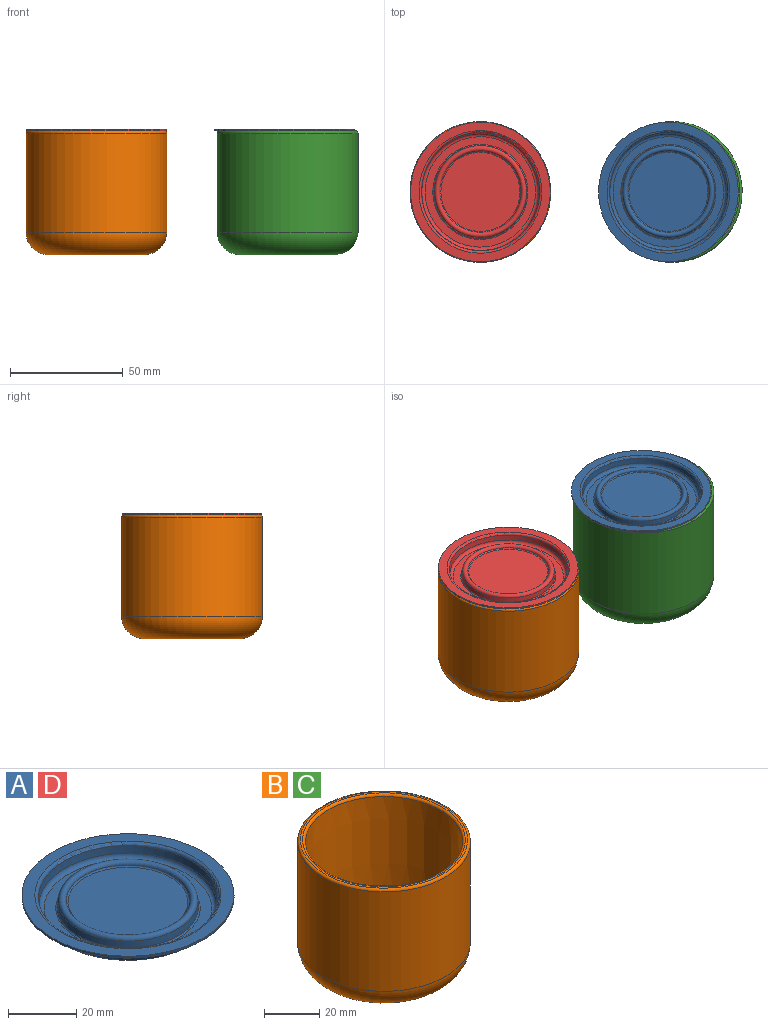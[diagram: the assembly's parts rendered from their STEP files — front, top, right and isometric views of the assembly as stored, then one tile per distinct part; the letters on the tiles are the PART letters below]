
ASSEMBLY  parts=4 mates=4
PART A: 22 faces, bbox 62x62x5.5 mm
  f0: plane 35.45x35.45mm, normal (0,0,-1), area 987mm2, adj f17
  f1: cone r=18.64mm half-angle=5deg, axis (0,0,1), area 15.4mm2, adj f2,f17
  f2: torus R=19.23mm, axis (0,0,-1), area 179.3mm2, adj f1,f3
  f3: cone r=19.73mm half-angle=5deg, axis (0,0,-1), area 304.1mm2, adj f2,f16
  f4: plane 49.39x49.39mm, normal (0,0,-1), area 539mm2, adj f14,f16
  f5: cone r=26.53mm half-angle=5deg, axis (0,0,1), area 425.6mm2, adj f14,f21
  f6: plane 62x62mm, normal (0,0,-1), area 659.1mm2, adj f7,f21
  f7: cylinder r=31mm len=62mm, axis (0,0,-1), area 136.3mm2, adj f6,f8
  f8: plane 62x62mm, normal (0,0,1), area 690.5mm2, adj f7,f20
  f9: cone r=26.31mm half-angle=5deg, axis (0,0,1), area 414.8mm2, adj f15,f20
  f10: plane 49.03x49.03mm, normal (0,0,1), area 486.5mm2, adj f15,f19
  f11: cone r=20.66mm half-angle=5deg, axis (0,0,-1), area 291mm2, adj f12,f19
  f12: torus R=19.23mm, axis (0,0,-1), area 426mm2, adj f11,f18
  f13: plane 35.09x35.09mm, normal (0,0,1), area 966.8mm2, adj f18
  f14: torus R=24.7mm, axis (0,0,-1), area 483.4mm2, adj f4,f5
  f15: torus R=24.51mm, axis (0,0,1), area 355.7mm2, adj f9,f10
  f16: torus R=20.94mm, axis (0,0,-1), area 189.4mm2, adj f3,f4
  f17: torus R=17.73mm, axis (0,0,-1), area 171mm2, adj f0,f1
  f18: torus R=17.54mm, axis (0,0,1), area 81.5mm2, adj f12,f13
  f19: torus R=21.12mm, axis (0,0,1), area 97mm2, adj f10,f11
  f20: torus R=27.22mm, axis (0,0,1), area 248mm2, adj f8,f9
  f21: torus R=27.41mm, axis (0,0,-1), area 126.3mm2, adj f5,f6
PART B: 13 faces, bbox 67.6x67.6x55 mm
  f0: plane 60.5x60.5mm, normal (0,0,1), area 153.2mm2, adj f1,f12
  f1: torus R=29.43mm, axis (0,0,-1), area 281.1mm2, adj f0,f2
  f2: cone r=27.76mm half-angle=1deg, axis (0,0,1), area 6831.2mm2, adj f1,f3
  f3: torus R=17.76mm, axis (0,0,-1), area 2350.6mm2, adj f2,f4
  f4: plane 35.52x35.52mm, normal (0,0,1), area 990.8mm2, adj f3
  f5: plane 34.55x34.55mm, normal (0,0,-1), area 937.5mm2, adj f6
  f6: torus R=17.28mm, axis (0,0,-1), area 97mm2, adj f5,f7
  f7: cone r=18.7mm half-angle=40deg, axis (0,0,-1), area 118.4mm2, adj f6,f8
  f8: torus R=19.47mm, axis (0,0,-1), area 104.5mm2, adj f7,f9
  f9: plane 42.5x42.5mm, normal (0,0,-1), area 228.2mm2, adj f8,f10
  f10: torus R=21.25mm, axis (0,0,-1), area 2725.6mm2, adj f9,f11
  f11: cylinder r=31.25mm len=62.5mm, axis (0,0,-1), area 8639.4mm2, adj f10,f12
  f12: torus R=30.25mm, axis (0,0,-1), area 304.8mm2, adj f0,f11
PART C: same geometry as B
PART D: same geometry as A
PLACE A t=(79.02,10.44,42.23)mm
PLACE B t=(-4.48,10.44,-7.97)mm fixed
PLACE C t=(80.52,10.44,-7.97)mm fixed
PLACE D t=(-4.48,10.44,42.23)mm
MATE planar D.f1 <-> B.f1  axis (0,0,-1) through (-4.48,10.44,47.03)mm
MATE cylindrical D.f1 <-> B.f1  axis (0,0,1) through (-4.48,10.44,47.73)mm
MATE planar B.f1 <-> C.f1  axis (0,0,-1) through (-4.48,10.44,-7.97)mm
MATE planar A.f1 <-> C.f1  axis (0,0,-1) through (79.02,10.44,47.03)mm
